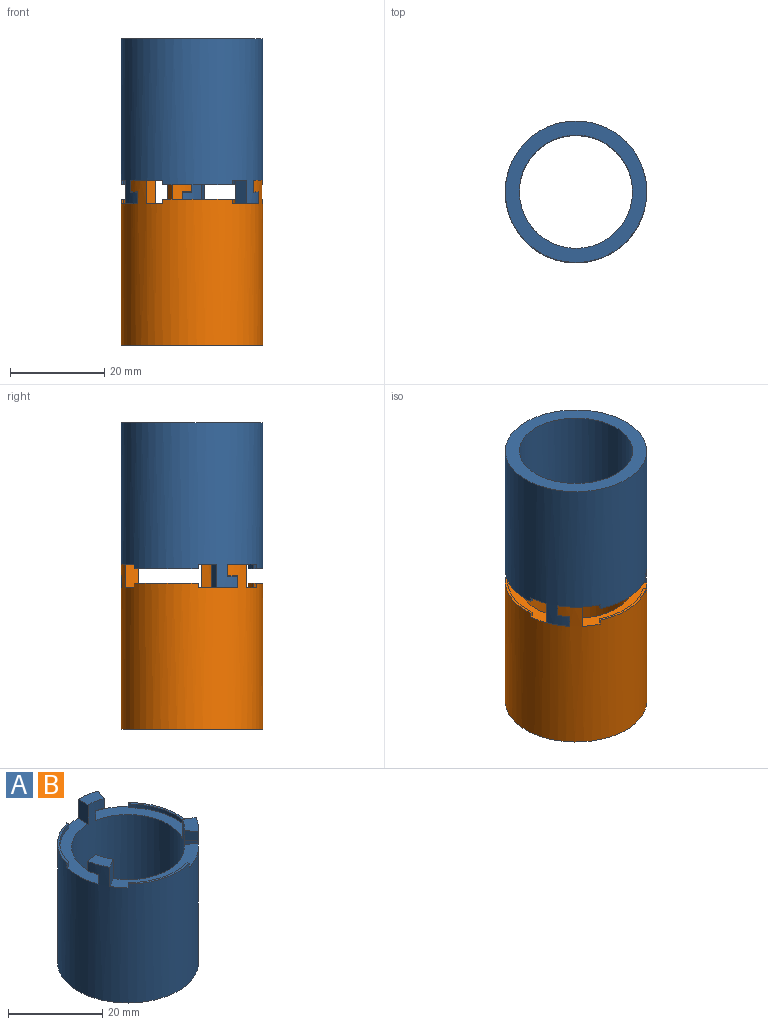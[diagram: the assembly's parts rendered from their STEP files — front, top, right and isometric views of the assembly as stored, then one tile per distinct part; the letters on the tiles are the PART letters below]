
ASSEMBLY  parts=2 mates=1
PART A: 33 faces, bbox 30x30x35 mm
  f0: plane 22.27x12.42mm, normal (0,0,1), area 70mm2, adj f2,f5,f8,f11,f25,f26,f27
  f1: plane 24.48x8.5mm, normal (0,0,1), area 70mm2, adj f2,f5,f6,f9,f21,f22,f23
  f2: cylinder r=15mm len=35mm, axis (0,0,-1), area 2933.5mm2, adj f0,f1,f3,f4,f6,f7,f8,f9
  f3: plane 20.13x15mm, normal (0,0,1), area 70mm2, adj f2,f5,f7,f10,f29,f30,f31
  f4: plane 30x30mm, normal (0,0,-1), area 254.5mm2, adj f2,f5
  f5: cylinder r=12mm len=35mm, axis (0,0,-1), area 2309.1mm2, adj f0,f1,f3,f4,f6,f7,f8,f9
  f6: plane 5x2.6mm, normal (0.5,-0.87,0), area 15mm2, adj f1,f2,f5,f14
  f7: plane 2.82x2.5mm, normal (-0.34,0.94,0), area 7.5mm2, adj f2,f3,f5,f12
  f8: plane 5x2.6mm, normal (0.5,0.87,0), area 15mm2, adj f0,f2,f5,f17
  f9: plane 2.5x2.3mm, normal (-0.64,-0.77,0), area 7.5mm2, adj f1,f2,f5,f15
  f10: plane 5x3mm, normal (-1,0,0), area 15mm2, adj f2,f3,f5,f20
  f11: plane 2.95x2.5mm, normal (0.98,-0.17,0), area 7.5mm2, adj f0,f2,f5,f18
  f12: plane 3.5x3.05mm, normal (0,0,-1), area 7.1mm2, adj f2,f5,f7,f13
  f13: plane 2.95x2.5mm, normal (-0.17,0.98,0), area 7.5mm2, adj f2,f5,f12,f14
  f14: plane 5.42x4.38mm, normal (0,0,1), area 14.1mm2, adj f2,f5,f6,f13
  f15: plane 3.78x3.78mm, normal (0,0,-1), area 7.1mm2, adj f2,f5,f9,f16
  f16: plane 2.5x2.3mm, normal (-0.77,-0.64,0), area 7.5mm2, adj f2,f5,f15,f17
  f17: plane 5.49x5.28mm, normal (0,0,1), area 14.1mm2, adj f2,f5,f8,f16
  f18: plane 3.5x3.05mm, normal (0,0,-1), area 7.1mm2, adj f2,f5,f11,f19
  f19: plane 2.82x2.5mm, normal (0.94,-0.34,0), area 7.5mm2, adj f2,f5,f18,f20
  f20: plane 5.13x3.72mm, normal (0,0,1), area 14.1mm2, adj f2,f5,f10,f19
  f21: cylinder r=14.5mm len=14.01mm, axis (0,0,-1), area 15.2mm2, adj f1,f22,f23,f24
  f22: plane 1x0.35mm, normal (-0.71,0.71,0), area 0.5mm2, adj f1,f2,f21,f24
  f23: plane 1x0.48mm, normal (0.97,0.26,0), area 0.5mm2, adj f1,f2,f21,f24
  f24: plane 14.49x4.75mm, normal (0,0,1), area 7.7mm2, adj f2,f21,f22,f23
  f25: cylinder r=14.5mm len=14.01mm, axis (0,0,-1), area 15.2mm2, adj f0,f26,f27,f28
  f26: plane 1x0.48mm, normal (-0.26,-0.97,0), area 0.5mm2, adj f0,f2,f25,f28
  f27: plane 1x0.35mm, normal (-0.71,0.71,0), area 0.5mm2, adj f0,f2,f25,f28
  f28: plane 14.49x4.75mm, normal (0,0,1), area 7.7mm2, adj f2,f25,f26,f27
  f29: cylinder r=14.5mm len=10.25mm, axis (0,0,-1), area 15.2mm2, adj f3,f30,f31,f32
  f30: plane 1x0.48mm, normal (0.97,0.26,0), area 0.5mm2, adj f2,f3,f29,f32
  f31: plane 1x0.48mm, normal (-0.26,-0.97,0), area 0.5mm2, adj f2,f3,f29,f32
  f32: plane 10.74x10.74mm, normal (0,0,1), area 7.7mm2, adj f2,f29,f30,f31
PART B: same geometry as A
PLACE A rot(axis=(0.09,1,0),180deg) t=(-6.12,9,70.48)mm
PLACE B rot(axis=(0,0,1),20deg) t=(-6.12,9,5.48)mm
MATE fastened B.f11 <-> A.f19  axis (0.98,0.17,0) through (-8.46,22.29,36.73)mm
